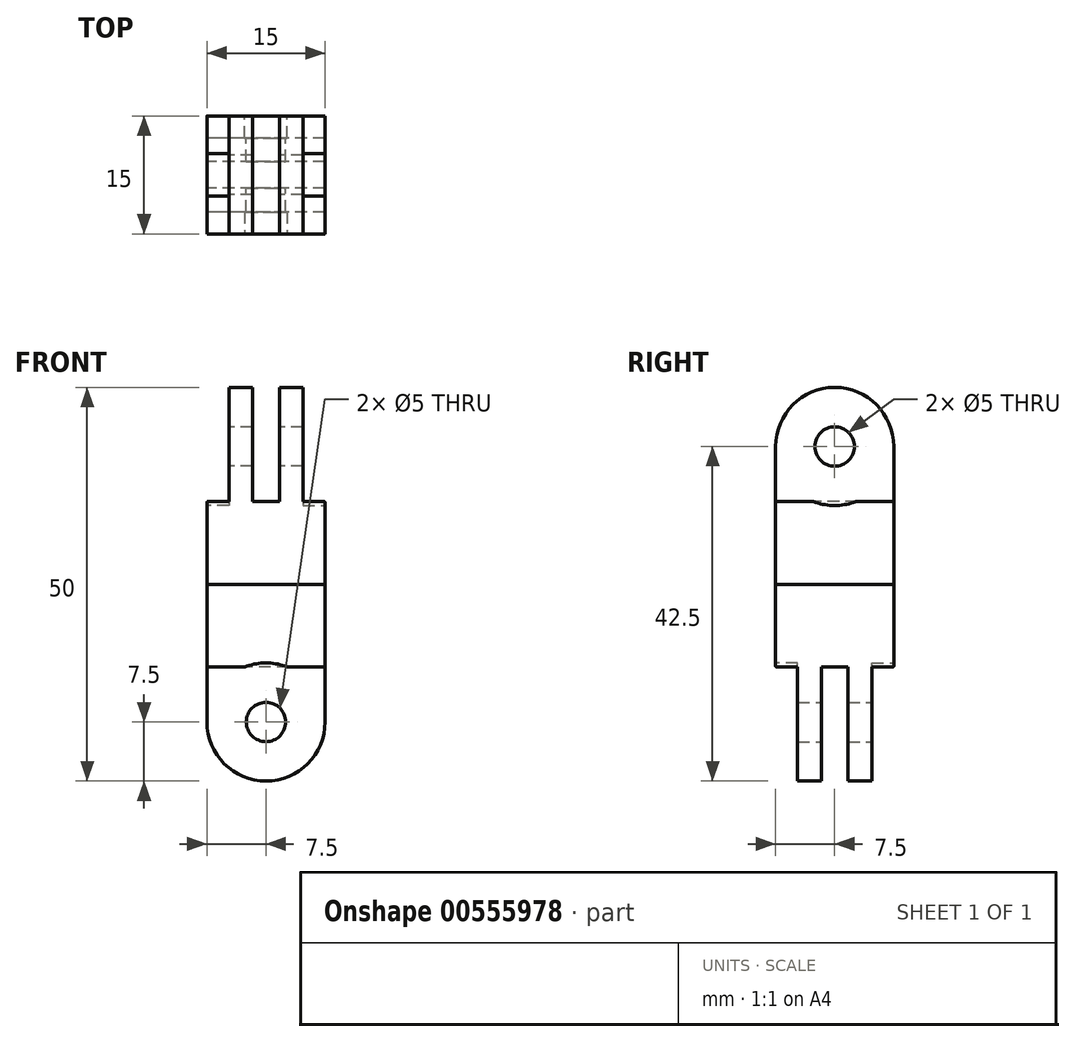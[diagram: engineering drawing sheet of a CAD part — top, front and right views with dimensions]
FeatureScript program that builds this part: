
annotation { "Feature Type Name" : "Feature", "Feature Type Description" : "" }
export const myFeature = defineFeature(function(context is Context, id is Id, definition is map)
    precondition{}
    {
        {
            assignVariable(context, id + "F0", {"name" : "length", "anyValue" : 5});
        }
        {
            var Q0;
            Q0=qCreatedBy(makeId("Right.planeOp"),FACE);
            var sketch = newSketch(context, id + "F1", { "sketchPlane" : qUnion([Q0])});
            skArc(sketch, "E0", {"start": v(7.5, 0) * mm, "mid": v(0, 7.5) * mm, "end": v(-7.5, 0) * mm});
            skCircle(sketch, "E1", {"center": v(0, 0) * mm, "radius": 2.5 * mm});
            skLineSegment(sketch, "E2", {"start": v(-7.5, 0) * mm, "end": v(-7.5, -12.5) * mm});
            skLineSegment(sketch, "E3", {"start": v(7.5, 0) * mm, "end": v(7.5, -12.5) * mm});
            skLineSegment(sketch, "E4", {"start": v(7.5, -12.5) * mm, "end": v(-7.5, -12.5) * mm});
            skSolve(sketch);
        }
        {
            var Q0;
            Q0=makeQuery(id+"F1.imprint","IMPRINT",FACE,{"disambiguationData":[TD([[makeQuery(id+"F1.imprint","IMPRINT",EDGE,{"derivedFrom":sQuery(id+"F1.wireOp",EDGE,"E0")}),1.0]])]});
            extrude(context, id + "F2", {"entities" : qUnion([Q0]), "depth" : 15 * mm, "symmetric" : true});
        }
        {
            var Q0;
            Q0=qCreatedBy(makeId("Front.planeOp"),FACE);
            var sketch = newSketch(context, id + "F3", { "sketchPlane" : qUnion([Q0])});
            skLineSegment(sketch, "E5", {"start": v(0, -18.95) * mm, "end": v(0, 19.26) * mm, "construction": true});
            skLineSegment(sketch, "E6", {"start": v(-12.45, 0) * mm, "end": v(16.05, 0) * mm, "construction": true});
            skLineSegment(sketch, "E7.0", {"start": v(-1.7, -7) * mm, "end": v(-1.7, 8.45) * mm});
            skLineSegment(sketch, "E8.0.MirrorCS", {"start": v(1.7, -7) * mm, "end": v(1.7, 8.45) * mm});
            skLineSegment(sketch, "E9.0", {"start": v(-8.58, -7) * mm, "end": v(-4.7, -7) * mm});
            skLineSegment(sketch, "E10.0", {"start": v(4.7, -7) * mm, "end": v(4.7, 8.45) * mm});
            skLineSegment(sketch, "E11.0", {"start": v(-4.7, -7) * mm, "end": v(-4.7, 8.45) * mm});
            skPoint(sketch, "E12.orphan", {"position": v(-1.7, -18.95) * mm});
            skLineSegment(sketch, "E13.trimOffspring", {"start": v(4.7, -7) * mm, "end": v(8.53, -7) * mm});
            skPoint(sketch, "E14.orphan", {"position": v(1.7, -18.95) * mm});
            skLineSegment(sketch, "E15", {"start": v(-8.58, 8.45) * mm, "end": v(-4.7, 8.45) * mm});
            skLineSegment(sketch, "E16", {"start": v(8.53, 8.45) * mm, "end": v(8.53, -7) * mm});
            skLineSegment(sketch, "E17", {"start": v(-8.58, -7) * mm, "end": v(-8.58, 8.45) * mm});
            skLineSegment(sketch, "E18.trimOffspring", {"start": v(-1.7, 8.45) * mm, "end": v(1.7, 8.45) * mm});
            skPoint(sketch, "E19.orphan", {"position": v(-1.7, 19.26) * mm});
            skPoint(sketch, "E20.orphan", {"position": v(1.7, 19.26) * mm});
            skLineSegment(sketch, "E21.trimOffspring", {"start": v(4.7, 8.45) * mm, "end": v(8.53, 8.45) * mm});
            skLineSegment(sketch, "E22", {"start": v(1.7, -7) * mm, "end": v(-1.7, -7) * mm});
            skSolve(sketch);
        }
        {
            var Q0;
            {Q0=qUnion([makeQuery(id+"F3.imprint","IMPRINT",FACE,{"disambiguationData":[TD([[makeQuery(id+"F3.imprint","IMPRINT",EDGE,{"derivedFrom":sQuery(id+"F3.wireOp",EDGE,"E7.0")}),-1.0]])]}),makeQuery(id+"F3.imprint","IMPRINT",FACE,{"disambiguationData":[TD([[makeQuery(id+"F3.imprint","IMPRINT",EDGE,{"derivedFrom":sQuery(id+"F3.wireOp",EDGE,"E9.0")}),1.0]])]}),makeQuery(id+"F3.imprint","IMPRINT",FACE,{"disambiguationData":[TD([[makeQuery(id+"F3.imprint","IMPRINT",EDGE,{"derivedFrom":sQuery(id+"F3.wireOp",EDGE,"E10.0")}),-1.0]])]})]);}
            extrude(context, id + "F4", {"entities" : qUnion([Q0]), "operationType" : NewBodyOperationType.REMOVE, "oppositeDirection" : true, "depth" : 32.83 * mm, "symmetric" : true});
        }
        {
            var Q0;
            Q0=makeQuery(id+"F2.opExtrude","CAP_FACE",FACE,{"disambiguationData":[OSD([sQuery(id+"F1.wireOp",EDGE,"E0"),sQuery(id+"F1.wireOp",EDGE,"E1"),sQuery(id+"F1.wireOp",EDGE,"E2"),sQuery(id+"F1.wireOp",EDGE,"E3"),sQuery(id+"F1.wireOp",EDGE,"E4")])],"isStart":true});
            var sketch = newSketch(context, id + "F5", { "sketchPlane" : qUnion([Q0])});
            skCircle(sketch, "E23", {"center": v(0, 0) * mm, "radius": 7.5 * mm});
            skSolve(sketch);
        }
        {
            var Q0;
            {var subQ0=makeQuery(id+"F4.boolean.opBoolean","INTERSECT",EDGE,{"derivedFrom":[makeQuery(id+"F2.opExtrude","CAP_FACE",FACE,{"disambiguationData":[OSD([sQuery(id+"F1.wireOp",EDGE,"E0"),sQuery(id+"F1.wireOp",EDGE,"E1"),sQuery(id+"F1.wireOp",EDGE,"E2"),sQuery(id+"F1.wireOp",EDGE,"E3"),sQuery(id+"F1.wireOp",EDGE,"E4")])],"isStart":true}),makeQuery(id+"F4.opExtrude","SWEPT_FACE",FACE,{"disambiguationData":[OSD([sQuery(id+"F3.wireOp",EDGE,"E9.0")])]})]});var subQ1=sQuery(id+"F5.wireOp",EDGE,"E23");var subQ3=makeQuery(id+"F5.imprint","INTERSECT",VERTEX,{"disambiguationData":[OD(0.0)],"derivedFrom":[subQ0,subQ1]});Q0=qUnion([makeQuery(id+"F5.imprint","IMPRINT",FACE,{"disambiguationData":[TD([[makeQuery(id+"F5.imprint","IMPRINT",EDGE,{"disambiguationData":[TD([[subQ3,-1.0]])],"derivedFrom":subQ1}),1.0]])]}),makeQuery(id+"F5.imprint","IMPRINT",FACE,{"disambiguationData":[TD([[makeQuery(id+"F5.imprint","IMPRINT",EDGE,{"disambiguationData":[TD([[subQ3,1.0]])],"derivedFrom":subQ1}),1.0]])]})]);}
            var Q1;
            Q1=makeQuery(id+"F4.boolean.opBoolean","COPY",FACE,{"derivedFrom":makeQuery(id+"F4.opExtrude","SWEPT_FACE",FACE,{"disambiguationData":[OSD([sQuery(id+"F3.wireOp",EDGE,"E11.0")])]})});
            extrude(context, id + "F6", {"entities" : qUnion([Q0]), "operationType" : NewBodyOperationType.REMOVE, "endBound" : BoundingType.UP_TO_SURFACE, "oppositeDirection" : true, "endBoundEntityFace" : qUnion([Q1]), "depth" : 25 * mm});
        }
        {
            var Q0;
            Q0=makeQuery(id+"F2.opExtrude","CAP_FACE",FACE,{"disambiguationData":[OSD([sQuery(id+"F1.wireOp",EDGE,"E0"),sQuery(id+"F1.wireOp",EDGE,"E1"),sQuery(id+"F1.wireOp",EDGE,"E2"),sQuery(id+"F1.wireOp",EDGE,"E3"),sQuery(id+"F1.wireOp",EDGE,"E4")])],"isStart":false});
            var sketch = newSketch(context, id + "F7", { "sketchPlane" : qUnion([Q0])});
            skCircle(sketch, "E24", {"center": v(0, 0) * mm, "radius": 7.5 * mm});
            skSolve(sketch);
        }
        {
            var Q0;
            {var subQ0=makeQuery(id+"F4.boolean.opBoolean","INTERSECT",EDGE,{"derivedFrom":[makeQuery(id+"F2.opExtrude","CAP_FACE",FACE,{"disambiguationData":[OSD([sQuery(id+"F1.wireOp",EDGE,"E0"),sQuery(id+"F1.wireOp",EDGE,"E1"),sQuery(id+"F1.wireOp",EDGE,"E2"),sQuery(id+"F1.wireOp",EDGE,"E3"),sQuery(id+"F1.wireOp",EDGE,"E4")])],"isStart":false}),makeQuery(id+"F4.opExtrude","SWEPT_FACE",FACE,{"disambiguationData":[OSD([sQuery(id+"F3.wireOp",EDGE,"E13.trimOffspring")])]})]});var subQ1=sQuery(id+"F7.wireOp",EDGE,"E24");var subQ3=makeQuery(id+"F7.imprint","INTERSECT",VERTEX,{"disambiguationData":[OD(0.0)],"derivedFrom":[subQ0,subQ1]});Q0=qUnion([makeQuery(id+"F7.imprint","IMPRINT",FACE,{"disambiguationData":[TD([[makeQuery(id+"F7.imprint","IMPRINT",EDGE,{"disambiguationData":[TD([[subQ3,1.0]])],"derivedFrom":subQ1}),1.0]])]}),makeQuery(id+"F7.imprint","IMPRINT",FACE,{"disambiguationData":[TD([[makeQuery(id+"F7.imprint","IMPRINT",EDGE,{"disambiguationData":[TD([[subQ3,-1.0]])],"derivedFrom":subQ1}),1.0]])]})]);}
            var Q1;
            Q1=makeQuery(id+"F4.boolean.opBoolean","COPY",FACE,{"derivedFrom":makeQuery(id+"F4.opExtrude","SWEPT_FACE",FACE,{"disambiguationData":[OSD([sQuery(id+"F3.wireOp",EDGE,"E10.0")])]})});
            extrude(context, id + "F8", {"entities" : qUnion([Q0]), "operationType" : NewBodyOperationType.REMOVE, "endBound" : BoundingType.UP_TO_SURFACE, "oppositeDirection" : true, "endBoundEntityFace" : qUnion([Q1]), "depth" : 25 * mm});
        }
        {
            var Q0;
            {var subQ0=sQuery(id+"F1.wireOp",EDGE,"E2");var subQ1=makeQuery(id+"F2.opExtrude","CAP_FACE",FACE,{"disambiguationData":[OSD([sQuery(id+"F1.wireOp",EDGE,"E0"),sQuery(id+"F1.wireOp",EDGE,"E1"),subQ0,sQuery(id+"F1.wireOp",EDGE,"E3"),sQuery(id+"F1.wireOp",EDGE,"E4")])],"isStart":false});var subQ2=makeQuery(id+"F4.opExtrude","SWEPT_FACE",FACE,{"disambiguationData":[OSD([sQuery(id+"F3.wireOp",EDGE,"E13.trimOffspring")])]});Q0=makeQuery(id+"F8.boolean.opBoolean","SPLIT",EDGE,{"disambiguationData":[TD([makeQuery(id+"F2.opExtrude","SWEPT_FACE",FACE,{"disambiguationData":[OSD([subQ0])]})])],"derivedFrom":makeQuery(id+"F4.boolean.opBoolean","INTERSECT",EDGE,{"derivedFrom":[subQ1,subQ2]})});}
            var Q1;
            Q1=makeQuery(id+"F8.boolean.opBoolean","COPY",EDGE,{"derivedFrom":makeQuery(id+"F8.opExtrude","CAP_EDGE",EDGE,{"disambiguationData":[OSD([sQuery(id+"F7.wireOp",EDGE,"E24")])],"isStart":true})});
            var Q2;
            {var subQ0=sQuery(id+"F1.wireOp",EDGE,"E3");var subQ1=makeQuery(id+"F2.opExtrude","CAP_FACE",FACE,{"disambiguationData":[OSD([sQuery(id+"F1.wireOp",EDGE,"E0"),sQuery(id+"F1.wireOp",EDGE,"E1"),sQuery(id+"F1.wireOp",EDGE,"E2"),subQ0,sQuery(id+"F1.wireOp",EDGE,"E4")])],"isStart":false});var subQ2=makeQuery(id+"F4.opExtrude","SWEPT_FACE",FACE,{"disambiguationData":[OSD([sQuery(id+"F3.wireOp",EDGE,"E13.trimOffspring")])]});Q2=makeQuery(id+"F8.boolean.opBoolean","SPLIT",EDGE,{"disambiguationData":[TD([makeQuery(id+"F2.opExtrude","SWEPT_FACE",FACE,{"disambiguationData":[OSD([subQ0])]})])],"derivedFrom":makeQuery(id+"F4.boolean.opBoolean","INTERSECT",EDGE,{"derivedFrom":[subQ1,subQ2]})});}
            var Q3;
            {var subQ0=sQuery(id+"F1.wireOp",EDGE,"E3");var subQ1=makeQuery(id+"F2.opExtrude","CAP_FACE",FACE,{"disambiguationData":[OSD([sQuery(id+"F1.wireOp",EDGE,"E0"),sQuery(id+"F1.wireOp",EDGE,"E1"),sQuery(id+"F1.wireOp",EDGE,"E2"),subQ0,sQuery(id+"F1.wireOp",EDGE,"E4")])],"isStart":true});var subQ2=makeQuery(id+"F4.opExtrude","SWEPT_FACE",FACE,{"disambiguationData":[OSD([sQuery(id+"F3.wireOp",EDGE,"E9.0")])]});Q3=makeQuery(id+"F6.boolean.opBoolean","SPLIT",EDGE,{"disambiguationData":[TD([makeQuery(id+"F2.opExtrude","SWEPT_FACE",FACE,{"disambiguationData":[OSD([subQ0])]})])],"derivedFrom":makeQuery(id+"F4.boolean.opBoolean","INTERSECT",EDGE,{"derivedFrom":[subQ1,subQ2]})});}
            var Q4;
            Q4=makeQuery(id+"F6.boolean.opBoolean","COPY",EDGE,{"derivedFrom":makeQuery(id+"F6.opExtrude","CAP_EDGE",EDGE,{"disambiguationData":[OSD([sQuery(id+"F5.wireOp",EDGE,"E23")])],"isStart":true})});
            var Q5;
            {var subQ0=sQuery(id+"F1.wireOp",EDGE,"E2");var subQ1=makeQuery(id+"F2.opExtrude","CAP_FACE",FACE,{"disambiguationData":[OSD([sQuery(id+"F1.wireOp",EDGE,"E0"),sQuery(id+"F1.wireOp",EDGE,"E1"),subQ0,sQuery(id+"F1.wireOp",EDGE,"E3"),sQuery(id+"F1.wireOp",EDGE,"E4")])],"isStart":true});var subQ2=makeQuery(id+"F4.opExtrude","SWEPT_FACE",FACE,{"disambiguationData":[OSD([sQuery(id+"F3.wireOp",EDGE,"E9.0")])]});Q5=makeQuery(id+"F6.boolean.opBoolean","SPLIT",EDGE,{"disambiguationData":[TD([makeQuery(id+"F2.opExtrude","SWEPT_FACE",FACE,{"disambiguationData":[OSD([subQ0])]})])],"derivedFrom":makeQuery(id+"F4.boolean.opBoolean","INTERSECT",EDGE,{"derivedFrom":[subQ1,subQ2]})});}
            fillet(context, id + "F9", {"entities" : qUnion([Q0, Q1, Q2, Q3, Q4, Q5]), "radius" : .1 * mm, "tangentPropagation" : true, "allowEdgeOverflow" : false});
        }
        {
            var Q0;
            Q0=makeQuery(id+"F2.opExtrude","SWEPT_FACE",FACE,{"disambiguationData":[OSD([sQuery(id+"F1.wireOp",EDGE,"E4")])]});
            var sketch = newSketch(context, id + "F10", { "sketchPlane" : qUnion([Q0])});
            skLineSegment(sketch, "E25.bottom", {"start": v(7.5, 7.52) * mm, "end": v(-7.5, 7.52) * mm});
            skLineSegment(sketch, "E25.top", {"start": v(7.5, -7.52) * mm, "end": v(-7.5, -7.52) * mm});
            skLineSegment(sketch, "E25.left", {"start": v(7.5, 7.52) * mm, "end": v(7.5, -7.52) * mm});
            skLineSegment(sketch, "E25.right", {"start": v(-7.5, 7.52) * mm, "end": v(-7.5, -7.52) * mm});
            skPoint(sketch, "E25.middle", {"position": v(0, 0) * mm});
            skSolve(sketch);
        }
        {
            var Q0;
            {var subQ1=sQuery(id+"F1.wireOp",EDGE,"E4");var subQ2=makeQuery(id+"F2.opExtrude","SWEPT_EDGE",EDGE,{"disambiguationData":[OSD([sQuery(id+"F1.wireOp",EDGE,"E2"),subQ1])]});Q0=makeQuery(id+"F10.imprint","IMPRINT",FACE,{"disambiguationData":[TD([[makeQuery(id+"F10.imprint","IMPRINT",EDGE,{"derivedFrom":subQ2}),1.0]])]});}
            extrude(context, id + "F11", {"entities" : qUnion([Q0]), "operationType" : NewBodyOperationType.ADD, "depth" : (getVariable(context, 'length')) * mm, "offsetDistance" : 25 * mm});
        }
        {
            var Q0;
            Q0=makeQuery(id+"F2.opExtrude","SWEPT_BODY",BODY,{"disambiguationData":[OSD([sQuery(id+"F1.wireOp",EDGE,"E0"),sQuery(id+"F1.wireOp",EDGE,"E1"),sQuery(id+"F1.wireOp",EDGE,"E2"),sQuery(id+"F1.wireOp",EDGE,"E3"),sQuery(id+"F1.wireOp",EDGE,"E4")])]});
            var Q1;
            Q1=makeQuery(id+"F11.opExtrude","CAP_FACE",FACE,{"disambiguationData":[OSD([sQuery(id+"F1.wireOp",EDGE,"E2"),sQuery(id+"F1.wireOp",EDGE,"E3"),sQuery(id+"F1.wireOp",EDGE,"E4"),sQuery(id+"F10.wireOp",EDGE,"E25.left"),sQuery(id+"F10.wireOp",EDGE,"E25.right")])],"isStart":false});
            mirror(context, id + "F12", {"entities" : qUnion([Q0]), "mirrorPlane" : qUnion([Q1])});
        }
        {
            var Q0;
            Q0=qCreatedBy(makeId("Front.planeOp"),FACE);
            var sketch = newSketch(context, id + "F13", { "sketchPlane" : qUnion([Q0])});
            skLineSegment(sketch, "E26", {"start": v(0, 1.74) * mm, "end": v(0, -36.67) * mm});
            skPoint(sketch, "E26.endSnap0", {"position": v(0, -28) * mm});
            skSolve(sketch);
        }
        {
            var Q0;
            Q0=makeQuery(id+"F12.opPattern","COPY",BODY,{"derivedFrom":makeQuery(id+"F2.opExtrude","SWEPT_BODY",BODY,{"disambiguationData":[OSD([sQuery(id+"F1.wireOp",EDGE,"E0"),sQuery(id+"F1.wireOp",EDGE,"E1"),sQuery(id+"F1.wireOp",EDGE,"E2"),sQuery(id+"F1.wireOp",EDGE,"E3"),sQuery(id+"F1.wireOp",EDGE,"E4")])]}),"instanceName":"1"});
            var Q1;
            Q1=sQuery(id+"F13.wireOp",EDGE,"E26");
            transform(context, id + "F14", {"entities" : qUnion([Q0]), "transformType" : TransformType.ROTATION, "transformAxis" : qUnion([Q1]), "angle" : 90 * degree, "makeCopy" : false});
        }
    });
